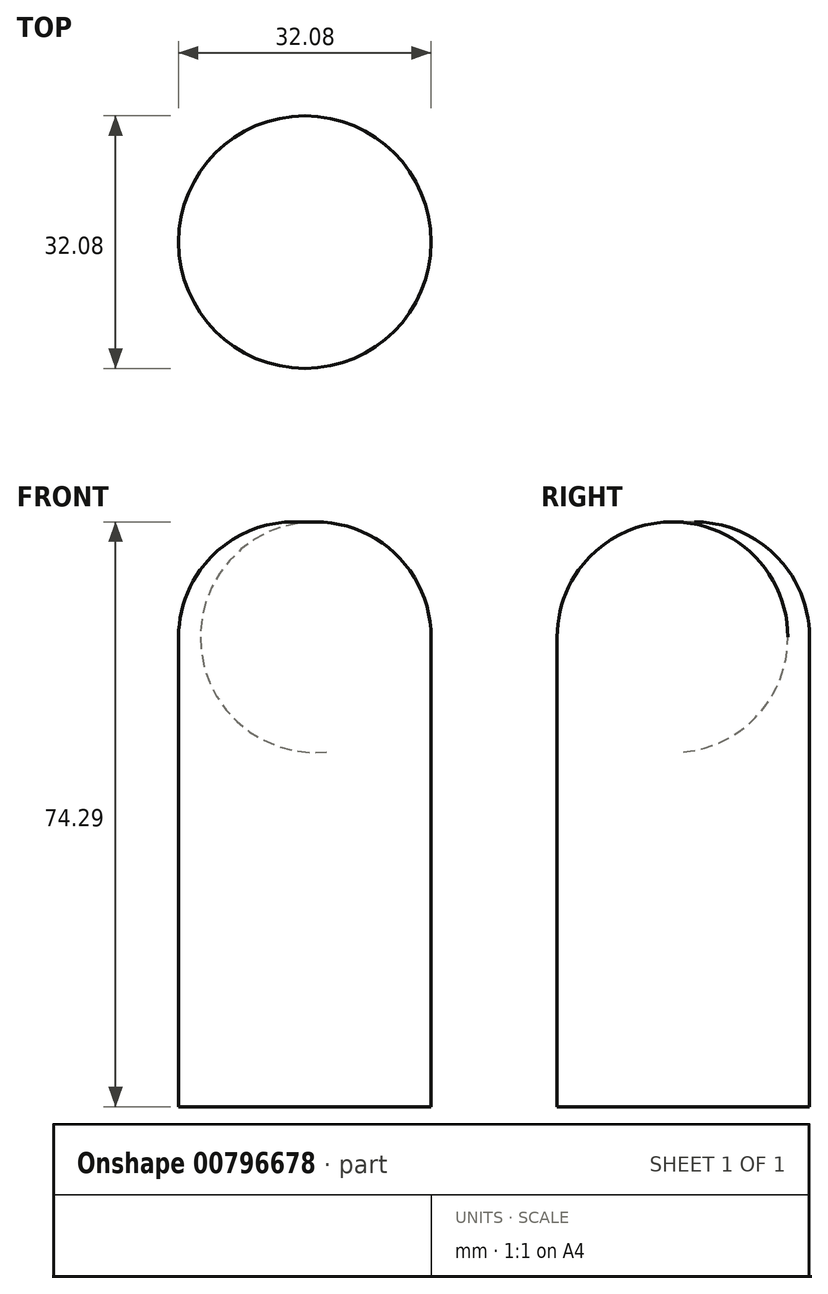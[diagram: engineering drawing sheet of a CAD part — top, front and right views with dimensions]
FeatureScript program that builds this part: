
annotation { "Feature Type Name" : "Feature", "Feature Type Description" : "" }
export const myFeature = defineFeature(function(context is Context, id is Id, definition is map)
    precondition{}
    {
        {
            var Q0;
            Q0=qCreatedBy(makeId("Front.planeOp"),FACE);
            var sketch = newSketch(context, id + "F0", { "sketchPlane" : qUnion([Q0])});
            skLineSegment(sketch, "E0", {"start": v(-16.04, -25.05) * mm, "end": v(-16.04, 34.58) * mm});
            skLineSegment(sketch, "E1", {"start": v(0, -25.05) * mm, "end": v(-16.04, -25.05) * mm});
            skFitSpline(sketch, "E2", {"points": [v(-16.04, 13.98) * mm, v(-37.26, 12.2) * mm, v(-40.33, 26.05) * mm], "startDerivative": vector(-37.81, -7.49) * mm, "endDerivative": vector(2.99, 36.48) * mm});
            skLineSegment(sketch, "E3", {"start": v(0, 63.26) * mm, "end": v(0, -56.45) * mm, "construction": true});
            skArc(sketch, "E4", {"start": v(0, 49.18) * mm, "mid": v(-11.24, 45.43) * mm, "end": v(-16.04, 34.58) * mm});
            skLineSegment(sketch, "E5", {"start": v(0, 49.18) * mm, "end": v(0, -25.05) * mm});
            skSolve(sketch);
        }
        {
            var Q0;
            Q0 = qSketchRegion(id + "F0", true);
            var Q1;
            Q1=sQuery(id+"F0.wireOp",EDGE,"E3");
            revolve(context, id + "F1", {"surfaceOperationType" : NewSurfaceOperationType.NEW, "entities" : qUnion([Q0]), "axis" : qUnion([Q1]), "revolveType" : RevolveType.FULL});
        }
    });
